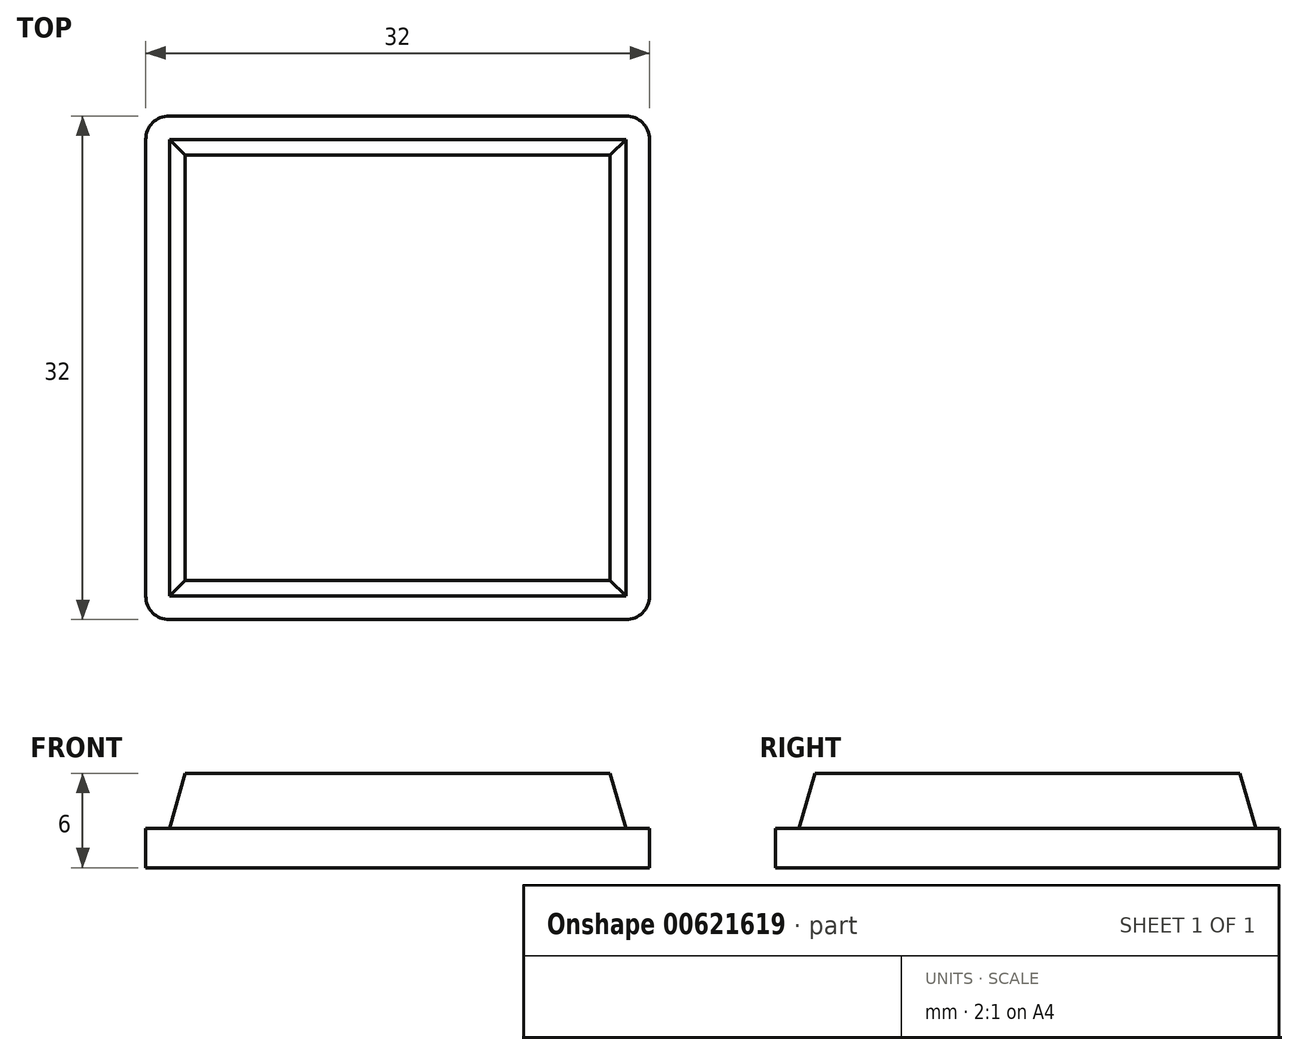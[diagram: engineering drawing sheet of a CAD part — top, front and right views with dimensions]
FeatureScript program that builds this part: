
annotation { "Feature Type Name" : "Feature", "Feature Type Description" : "" }
export const myFeature = defineFeature(function(context is Context, id is Id, definition is map)
    precondition{}
    {
        {
            var Q0;
            Q0=qCreatedBy(makeId("Top.planeOp"),FACE);
            var sketch = newSketch(context, id + "F0", { "sketchPlane" : qUnion([Q0])});
            skLineSegment(sketch, "E0.bottom", {"start": v(-16, 16) * mm, "end": v(16, 16) * mm});
            skLineSegment(sketch, "E0.top", {"start": v(-16, -16) * mm, "end": v(16, -16) * mm});
            skLineSegment(sketch, "E0.left", {"start": v(-16, 16) * mm, "end": v(-16, -16) * mm});
            skLineSegment(sketch, "E0.right", {"start": v(16, 16) * mm, "end": v(16, -16) * mm});
            skPoint(sketch, "E0.middle", {"position": v(0, 0) * mm});
            skSolve(sketch);
        }
        {
            var Q0;
            Q0=makeQuery(id+"F0.imprint","IMPRINT",FACE,{"disambiguationData":[TD([[makeQuery(id+"F0.imprint","IMPRINT",EDGE,{"derivedFrom":sQuery(id+"F0.wireOp",EDGE,"E0.bottom")}),-1.0]])]});
            extrude(context, id + "F1", {"entities" : qUnion([Q0]), "depth" : 2.5 * mm, "offsetDistance" : 25 * mm});
        }
        {
            var Q0;
            Q0=makeQuery(id+"F1.opExtrude","CAP_FACE",FACE,{"disambiguationData":[OSD([sQuery(id+"F0.wireOp",EDGE,"E0.bottom"),sQuery(id+"F0.wireOp",EDGE,"E0.top"),sQuery(id+"F0.wireOp",EDGE,"E0.left"),sQuery(id+"F0.wireOp",EDGE,"E0.right")])],"isStart":false});
            var sketch = newSketch(context, id + "F2", { "sketchPlane" : qUnion([Q0])});
            skLineSegment(sketch, "E1.bottom", {"start": v(14.5, 14.5) * mm, "end": v(-14.5, 14.5) * mm});
            skLineSegment(sketch, "E1.top", {"start": v(14.5, -14.5) * mm, "end": v(-14.5, -14.5) * mm});
            skLineSegment(sketch, "E1.left", {"start": v(14.5, 14.5) * mm, "end": v(14.5, -14.5) * mm});
            skLineSegment(sketch, "E1.right", {"start": v(-14.5, 14.5) * mm, "end": v(-14.5, -14.5) * mm});
            skPoint(sketch, "E1.middle", {"position": v(0, 0) * mm});
            skSolve(sketch);
        }
        {
            var Q0;
            Q0=qCreatedBy(makeId("Top.planeOp"),FACE);
            cPlane(context, id + "F3", {"entities" : qUnion([Q0]), "cplaneType" : CPlaneType.OFFSET, "offset" : 6 * mm, "width" : 150 * mm, "height" : 150 * mm});
        }
        {
            var Q0;
            Q0=qCreatedBy(id+"F3.planeOp",FACE);
            var sketch = newSketch(context, id + "F4", { "sketchPlane" : qUnion([Q0])});
            skLineSegment(sketch, "E2.bottom", {"start": v(-13.5, 13.5) * mm, "end": v(13.5, 13.5) * mm});
            skLineSegment(sketch, "E2.top", {"start": v(-13.5, -13.5) * mm, "end": v(13.5, -13.5) * mm});
            skLineSegment(sketch, "E2.left", {"start": v(-13.5, 13.5) * mm, "end": v(-13.5, -13.5) * mm});
            skLineSegment(sketch, "E2.right", {"start": v(13.5, 13.5) * mm, "end": v(13.5, -13.5) * mm});
            skPoint(sketch, "E2.middle", {"position": v(0, 0) * mm});
            skSolve(sketch);
        }
        {
            var Q1;
            Q1=makeQuery(id+"F2.imprint","IMPRINT",FACE,{"disambiguationData":[TD([[makeQuery(id+"F2.imprint","IMPRINT",EDGE,{"derivedFrom":sQuery(id+"F2.wireOp",EDGE,"E1.bottom")}),1.0]])]});
            var Q2;
            Q2=makeQuery(id+"F4.imprint","IMPRINT",FACE,{"disambiguationData":[TD([[makeQuery(id+"F4.imprint","IMPRINT",EDGE,{"derivedFrom":sQuery(id+"F4.wireOp",EDGE,"E2.bottom")}),-1.0]])]});
            loft(context, id + "F5", {"operationType" : NewBodyOperationType.ADD, "sheetProfilesArray" : [{ "sheetProfileEntities" : qUnion([Q1]) }, { "sheetProfileEntities" : qUnion([Q2]) }]});
        }
        {
            var Q0;
            Q0=makeQuery(id+"F1.opExtrude","SWEPT_EDGE",EDGE,{"disambiguationData":[OSD([sQuery(id+"F0.wireOp",EDGE,"E0.bottom"),sQuery(id+"F0.wireOp",EDGE,"E0.right")])]});
            var Q1;
            Q1=makeQuery(id+"F1.opExtrude","SWEPT_EDGE",EDGE,{"disambiguationData":[OSD([sQuery(id+"F0.wireOp",EDGE,"E0.top"),sQuery(id+"F0.wireOp",EDGE,"E0.right")])]});
            var Q2;
            Q2=makeQuery(id+"F1.opExtrude","SWEPT_EDGE",EDGE,{"disambiguationData":[OSD([sQuery(id+"F0.wireOp",EDGE,"E0.bottom"),sQuery(id+"F0.wireOp",EDGE,"E0.left")])]});
            var Q3;
            Q3=makeQuery(id+"F1.opExtrude","SWEPT_EDGE",EDGE,{"disambiguationData":[OSD([sQuery(id+"F0.wireOp",EDGE,"E0.top"),sQuery(id+"F0.wireOp",EDGE,"E0.left")])]});
            fillet(context, id + "F6", {"entities" : qUnion([Q0, Q1, Q2, Q3]), "radius" : 1.5 * mm, "allowEdgeOverflow" : false});
        }
    });
